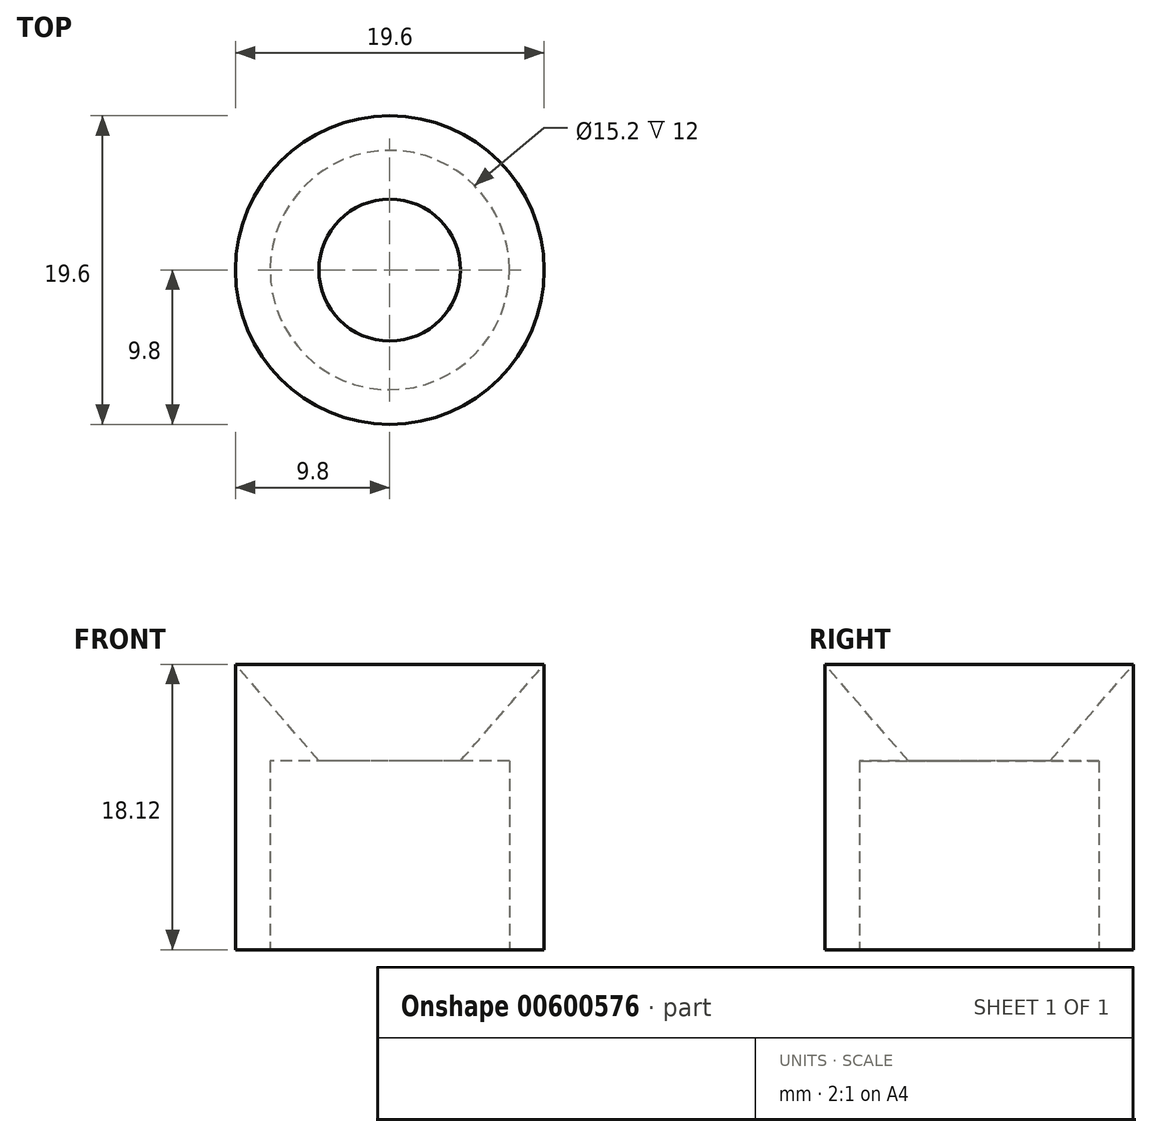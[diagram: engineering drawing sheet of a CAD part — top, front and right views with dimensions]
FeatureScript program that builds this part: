
annotation { "Feature Type Name" : "Feature", "Feature Type Description" : "" }
export const myFeature = defineFeature(function(context is Context, id is Id, definition is map)
    precondition{}
    {
        {
            var Q0;
            Q0=qCreatedBy(makeId("Top.planeOp"),FACE);
            var sketch = newSketch(context, id + "F0", { "sketchPlane" : qUnion([Q0])});
            skCircle(sketch, "E0", {"center": v(0, 0) * mm, "radius": 7.6 * mm});
            skCircle(sketch, "E1", {"center": v(0, 0) * mm, "radius": 9.8 * mm});
            skSolve(sketch);
        }
        {
            var Q0;
            Q0=qCreatedBy(makeId("Front.planeOp"),FACE);
            var sketch = newSketch(context, id + "F1", { "sketchPlane" : qUnion([Q0])});
            skLineSegment(sketch, "E2", {"start": v(0, 12) * mm, "end": v(4.5, 12) * mm});
            skLineSegment(sketch, "E3", {"start": v(4.5, 12) * mm, "end": v(9, 12) * mm});
            skLineSegment(sketch, "E4", {"start": v(0, 12) * mm, "end": v(9.8, 12) * mm});
            skLineSegment(sketch, "E5", {"start": v(9.8, 12) * mm, "end": v(9.8, 18.12) * mm});
            skLineSegment(sketch, "E6", {"start": v(4.5, 12) * mm, "end": v(9.8, 18.12) * mm});
            skSolve(sketch);
        }
        {
            var Q0;
            Q0=qCreatedBy(makeId("Front.planeOp"),FACE);
            var sketch = newSketch(context, id + "F2", { "sketchPlane" : qUnion([Q0])});
            skLineSegment(sketch, "E7", {"start": v(0, 14.21) * mm, "end": v(0, -26.25) * mm, "construction": true});
            skSolve(sketch);
        }
        {
            var Q0;
            Q0=qSketchRegion(id+"F0",true);
            extrude(context, id + "F3", {"entities" : qUnion([Q0]), "depth" : 12 * mm, "offsetDistance" : 25 * mm});
        }
        {
            var Q0;
            {var subQ0=sQuery(id+"F1.wireOp",EDGE,"E5");Q0=makeQuery(id+"F1.imprint","IMPRINT",FACE,{"disambiguationData":[TD([[makeQuery(id+"F1.imprint","IMPRINT",EDGE,{"derivedFrom":subQ0}),1.0]])]});}
            var Q1;
            Q1=sQuery(id+"F2.wireOp",EDGE,"E7");
            revolve(context, id + "F4", {"operationType" : NewBodyOperationType.ADD, "entities" : qUnion([Q0]), "axis" : qUnion([Q1]), "revolveType" : RevolveType.FULL});
        }
    });
